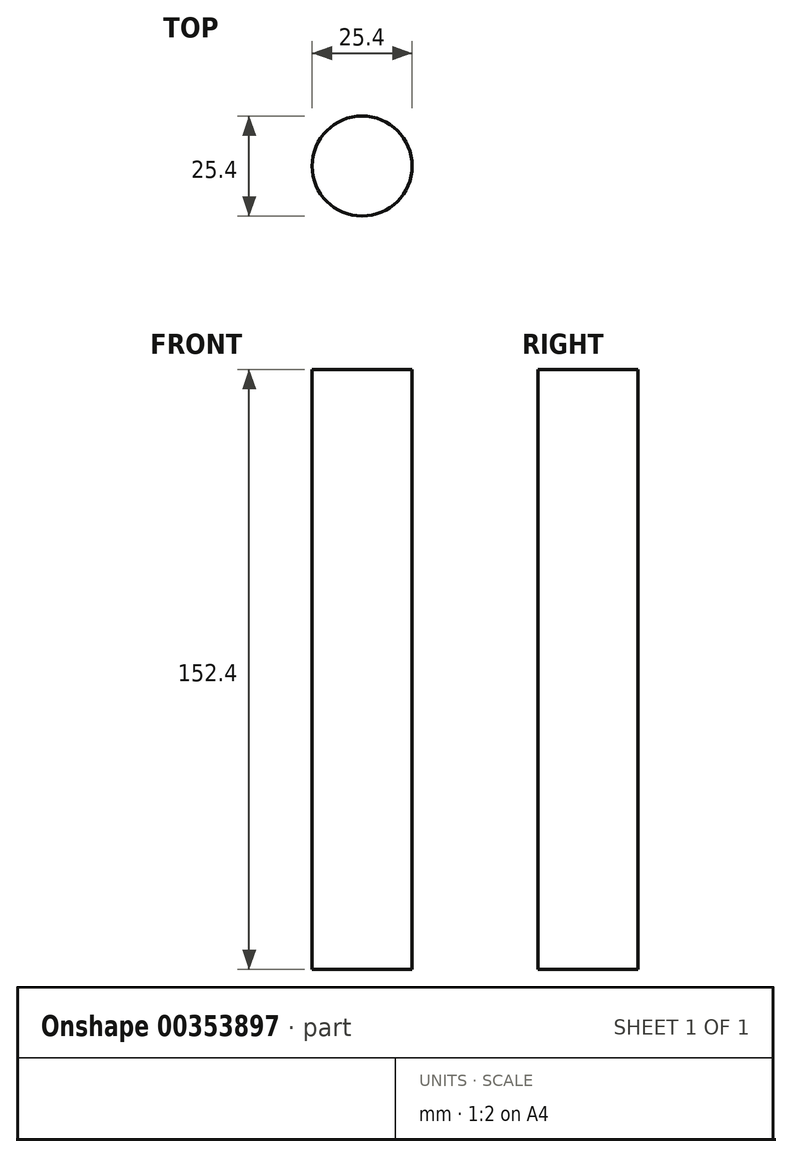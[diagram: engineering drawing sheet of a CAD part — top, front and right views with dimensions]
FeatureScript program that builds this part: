
annotation { "Feature Type Name" : "Feature", "Feature Type Description" : "" }
export const myFeature = defineFeature(function(context is Context, id is Id, definition is map)
    precondition{}
    {
        {
            var Q0;
            Q0=qCreatedBy(makeId("Top.planeOp"),FACE);
            var sketch = newSketch(context, id + "F0", { "sketchPlane" : qUnion([Q0])});
            skCircle(sketch, "E0", {"center": v(0, 0) * mm, "radius": 12.7 * mm});
            skSolve(sketch);
        }
        {
            var Q0;
            Q0 = qSketchRegion(id + "F0", true);
            var Q1;
            Q1=makeQuery(id+"F0.imprint","IMPRINT",FACE,{"disambiguationData":[TD([[makeQuery(id+"F0.imprint","IMPRINT",EDGE,{"derivedFrom":sQuery(id+"F0.wireOp",EDGE,"E0")}),1.0]])]});
            extrude(context, id + "F1", {"entities" : qUnion([Q0, Q1]), "endBound" : BoundingType.SYMMETRIC, "depth" : 152.4 * mm});
        }
    });
